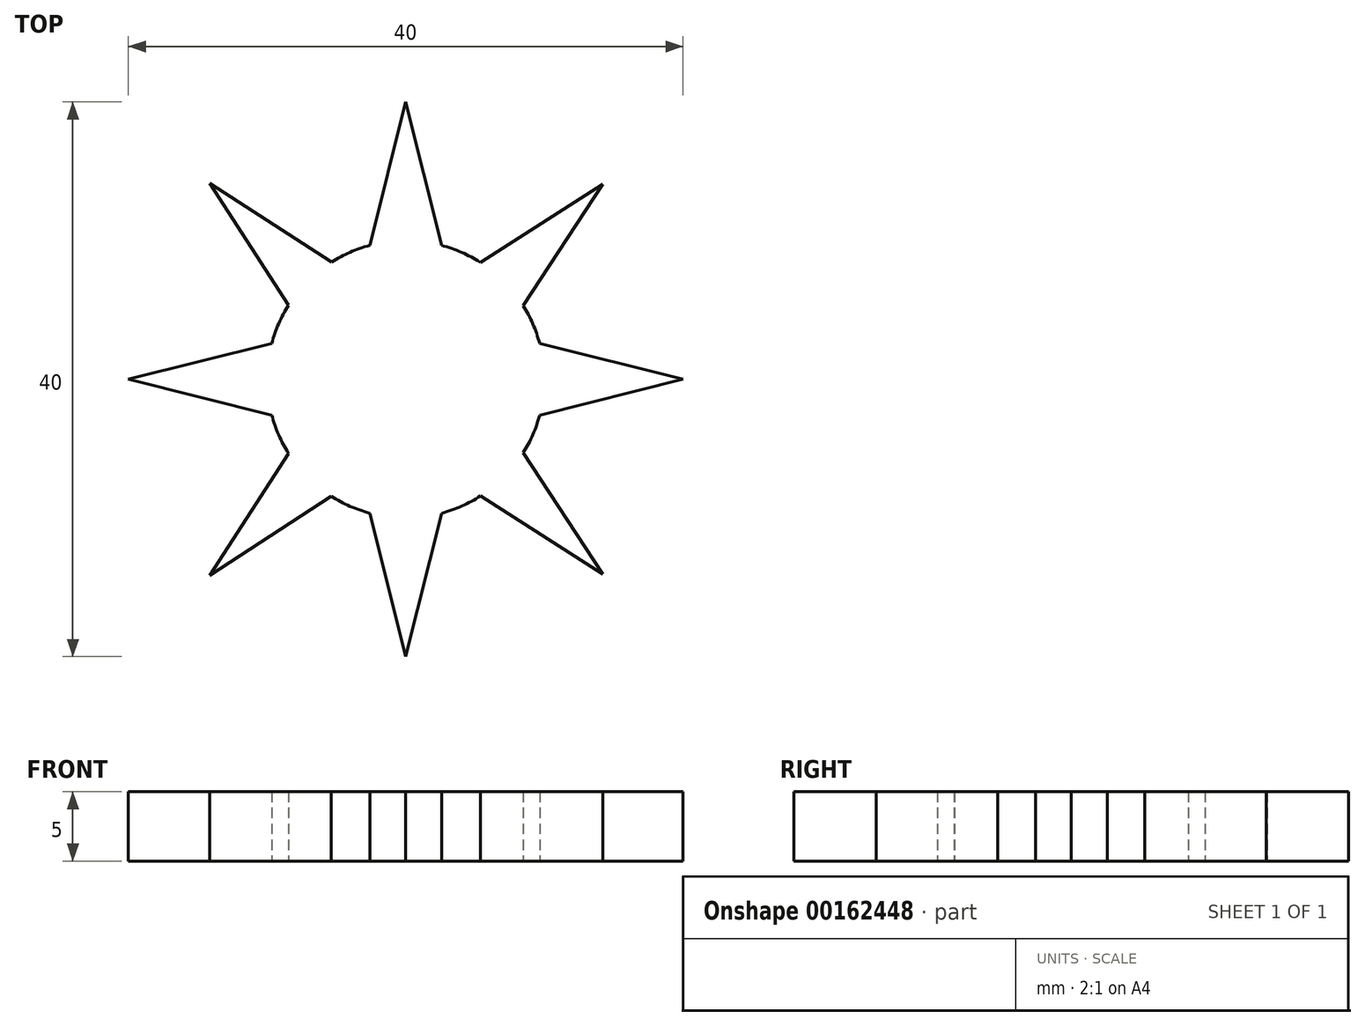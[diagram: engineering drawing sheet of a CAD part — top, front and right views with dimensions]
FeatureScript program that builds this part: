
annotation { "Feature Type Name" : "Feature", "Feature Type Description" : "" }
export const myFeature = defineFeature(function(context is Context, id is Id, definition is map)
    precondition{}
    {
        {
            var Q0;
            Q0=qCreatedBy(makeId("Top.planeOp"),FACE);
            var sketch = newSketch(context, id + "F0", { "sketchPlane" : qUnion([Q0])});
            skCircle(sketch, "E0", {"center": v(0, 0) * mm, "radius": 10 * mm});
            skSolve(sketch);
        }
        {
            var Q0;
            Q0 = qSketchRegion(id + "F0", true);
            extrude(context, id + "F1", {"entities" : qUnion([Q0]), "depth" : 5 * mm});
        }
        {
            var Q0;
            Q0=makeQuery(id+"F1.opExtrude","CAP_FACE",FACE,{"disambiguationData":[OSD([sQuery(id+"F0.wireOp",EDGE,"E0")])],"isStart":false});
            var sketch = newSketch(context, id + "F2", { "sketchPlane" : qUnion([Q0])});
            skCircle(sketch, "E1", {"center": v(0, 0) * mm, "radius": 0.83 * mm});
            skSolve(sketch);
        }
        {
            var Q0;
            Q0 = qSketchRegion(id + "F2", true);
            extrude(context, id + "F3", {"entities" : qUnion([Q0]), "operationType" : NewBodyOperationType.REMOVE, "endBound" : BoundingType.THROUGH_ALL, "oppositeDirection" : true, "depth" : 25 * mm, "hasDraft" : true, "draftAngle" : 3 * degree});
        }
        {
            var Q0;
            Q0=makeQuery(id+"F1.opExtrude","CAP_FACE",FACE,{"disambiguationData":[OSD([sQuery(id+"F0.wireOp",EDGE,"E0")])],"isStart":true});
            var sketch = newSketch(context, id + "F4", { "sketchPlane" : qUnion([Q0])});
            skLineSegment(sketch, "E2", {"start": v(-3.24, 7.05) * mm, "end": v(0, 20) * mm});
            skLineSegment(sketch, "E3", {"start": v(0, 20) * mm, "end": v(3.24, 7.03) * mm});
            skLineSegment(sketch, "E4", {"start": v(7.1, 3.22) * mm, "end": v(20, 0) * mm});
            skLineSegment(sketch, "E5", {"start": v(7.1, -3.22) * mm, "end": v(20, 0) * mm});
            skLineSegment(sketch, "E6", {"start": v(3.23, -7.06) * mm, "end": v(0, -20) * mm});
            skLineSegment(sketch, "E7", {"start": v(-3.23, -7.09) * mm, "end": v(0, -20) * mm});
            skLineSegment(sketch, "E8", {"start": v(-7.09, 3.23) * mm, "end": v(-20, 0) * mm});
            skLineSegment(sketch, "E9", {"start": v(-20, 0) * mm, "end": v(-7.09, -3.23) * mm});
            skPoint(sketch, "E10", {"position": v(20, 0) * mm});
            skLineSegment(sketch, "E11", {"start": v(-3.23, -7.09) * mm, "end": v(-14.14, -14.14) * mm});
            skLineSegment(sketch, "E12", {"start": v(-14.14, -14.14) * mm, "end": v(-7.09, -3.23) * mm});
            skLineSegment(sketch, "E13", {"start": v(-7.09, 3.23) * mm, "end": v(-14.14, 14.14) * mm});
            skLineSegment(sketch, "E14", {"start": v(-14.14, 14.14) * mm, "end": v(-3.24, 7.05) * mm});
            skLineSegment(sketch, "E15", {"start": v(3.24, 7.03) * mm, "end": v(14.21, 14.07) * mm});
            skLineSegment(sketch, "E16", {"start": v(14.21, 14.07) * mm, "end": v(7.1, 3.22) * mm});
            skLineSegment(sketch, "E17", {"start": v(7.1, -3.22) * mm, "end": v(14.21, -14.07) * mm});
            skLineSegment(sketch, "E18", {"start": v(3.23, -7.06) * mm, "end": v(14.21, -14.07) * mm});
            skSolve(sketch);
        }
        {
            var Q0;
            Q0 = qSketchRegion(id + "F4", true);
            extrude(context, id + "F5", {"entities" : qUnion([Q0]), "operationType" : NewBodyOperationType.ADD, "oppositeDirection" : true, "depth" : 5 * mm});
        }
    });
